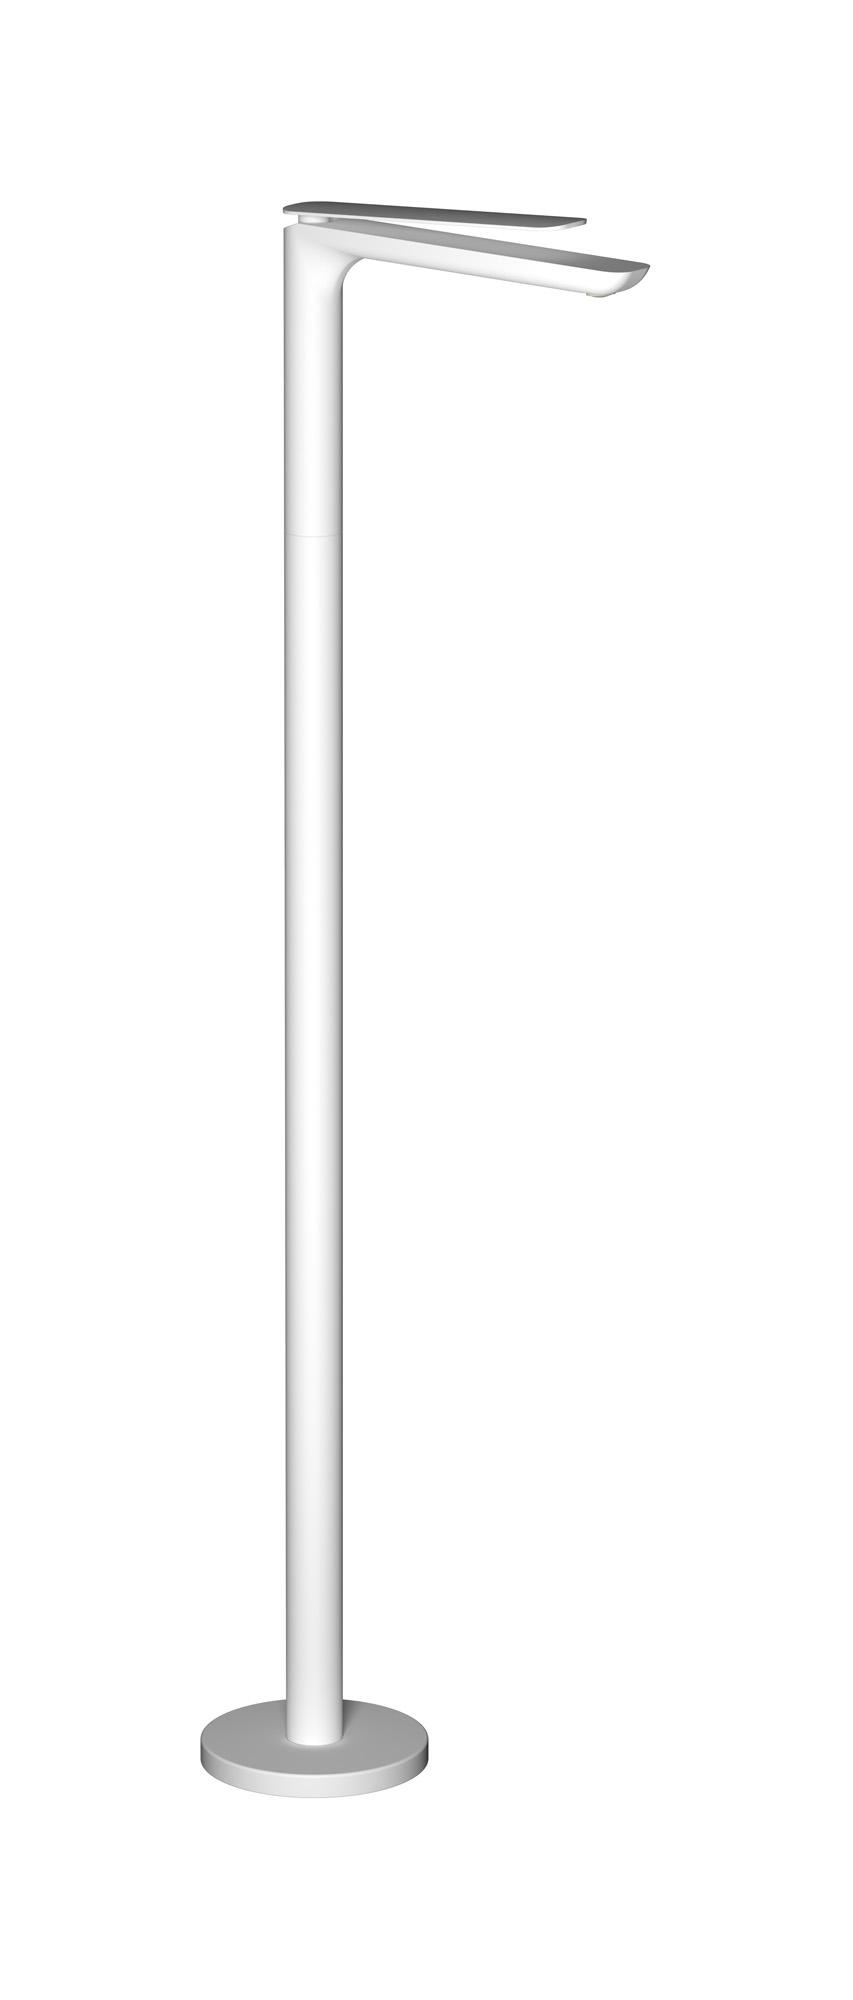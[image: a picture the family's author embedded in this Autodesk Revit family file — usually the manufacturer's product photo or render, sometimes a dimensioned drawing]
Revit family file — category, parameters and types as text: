
# Revit family: K2299
name_source: partatom
category: Apparecchi idraulici
units: mm (PartAtom-declared; Revit-internal decimal feet)

## family parameters
Basato su piano di lavoro = No
Condiviso = No
Mantieni orientamento annotazione = No
Numero OmniClass = 23.45.55.17
Punto di calcolo locali = No
Quota connettore circolare = Usa diametro
Sempre verticale = Sì
Taglio con vuoti quando caricato = No
Tipo di parte = Normale
Titolo OmniClass = Mixing Faucets

## types (9) — shared parameters
Cold water inlet = 10 mm  [stored 0.0328084 ft]
Commenti sul tipo = Washbasin mixer
Connessione CW = No
Connessione HW = No
Connessione di scarico = No
Connessione di ventilazione = No
Descrizione = Monohole freestanding washbasin mixer complete with drain
Hot water inlet = 10 mm  [stored 0.0328084 ft]
Produttore = IB Rubinetterie S.p.A.
URL = https://www.weareib.it
zero-valued in all types: Prospetto di default

## per-type parameters (varying)
| type | Finishes surface | Immagine tipo | Modello |
| Chrome | IB_Chrome | K2299CC.jpg | K2299CC |
| Brushed nickel | IB_Brushed nickel | K2299SS.jpg | K2299SS |
| Matt black | IB_matt black | K2299NP.jpg | K2299NP |
| Matt white | IB_matt white | K2299BO.jpg | K2299BO |
| Platinum | IB_Platinum | K2299PL.jpg | K2299PL |
| Pale gold | IB_Pale gold | K2299II.jpg | K2299II |
| Brushed pale gold | IB_brushed pale gold | K2299IS.jpg | K2299IS |
| Rose gold | IB_Rose gold | K2299RS.jpg | K2299RS |
| Gold | IB_gold | K2299OO.jpg | K2299OO |

note: [stored X ft] marks values corroborated as IEEE doubles in the binary element streams (Revit-internal decimal feet)
